# Revit family: 3-54-xxxx - Zora Vanity
name_source: partatom
category: Lighting Fixtures
revit_build: Autodesk Revit 2018 (Build: 20170223_1515(x64)
units: mm (PartAtom-declared; Revit-internal decimal feet)

## family parameters
Always vertical = Yes
Cut with Voids When Loaded = No
Host = Wall
Light Source = Yes
OmniClass Number = 23.80.70.00
OmniClass Title = Lighting
Part Type = Normal
Room Calculation Point = No
Round Connector Dimension = Use Diameter
Shared = No

## types (2) — shared parameters
Color Filter = 16777215
Dimming Lamp Color Temperature Shift = <None>
Lamp = LED Array
Light Source Symbol Size = 2 '
Manufacturer = Oxygen - Lighting & Fans
Metal Finish 1 = 50 - Industrial Brass
Model = 3-54-xxxx / Zora Vanity
References = Ref. 3 = 120 V / Ref. 37 = 277 V
Voltage = 120 V
Voltage Input = 120 V or 277 V - 50/60 Hz
Wattage Comments = 1 x 18W at 120

## per-type parameters (varying)
| type | Metal Finish 2 | URL |
| 3-54-650 / White - Industrial Brass | 6 - White |  |
| 3-54-1550 / Black - Industrial Brass | 15 - Black | www.oxygenlighting.com |

## geometry (parser evidence)
native form markers: Sweep x2
no freeform markers — native parametric forms only
